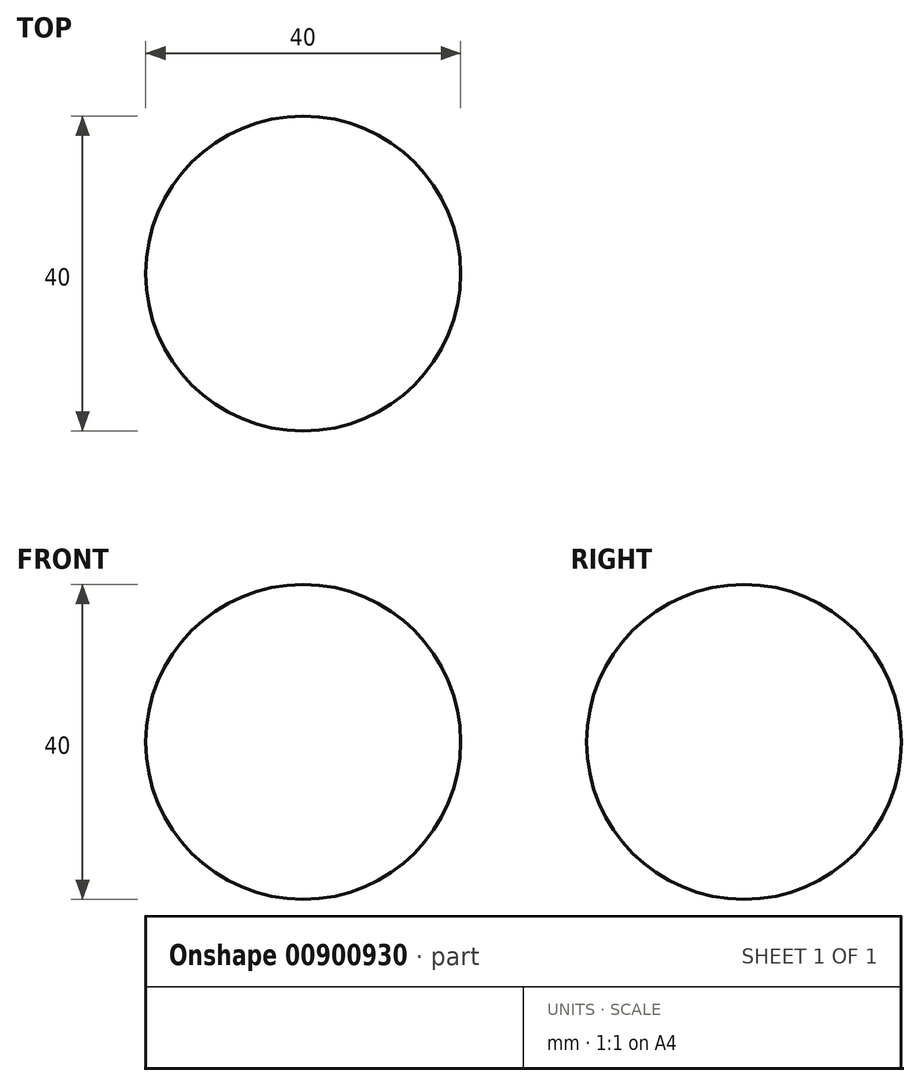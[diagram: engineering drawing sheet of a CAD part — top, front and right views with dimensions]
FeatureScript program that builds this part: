
annotation { "Feature Type Name" : "Feature", "Feature Type Description" : "" }
export const myFeature = defineFeature(function(context is Context, id is Id, definition is map)
    precondition{}
    {
        {
            var Q0;
            Q0=qCreatedBy(makeId("Front.planeOp"),FACE);
            var sketch = newSketch(context, id + "F0", { "sketchPlane" : qUnion([Q0])});
            skArc(sketch, "E0", {"start": v(0, -20) * mm, "mid": v(20, 0) * mm, "end": v(0, 20) * mm});
            skLineSegment(sketch, "E1", {"start": v(0, -20) * mm, "end": v(0, 20) * mm});
            skSolve(sketch);
        }
        {
            var Q0;
            Q0 = qSketchRegion(id + "F0", true);
            var Q1;
            Q1=sQuery(id+"F0.wireOp",EDGE,"E1");
            revolve(context, id + "F1", {"surfaceOperationType" : NewSurfaceOperationType.NEW, "entities" : qUnion([Q0]), "axis" : qUnion([Q1]), "revolveType" : RevolveType.FULL});
        }
    });
